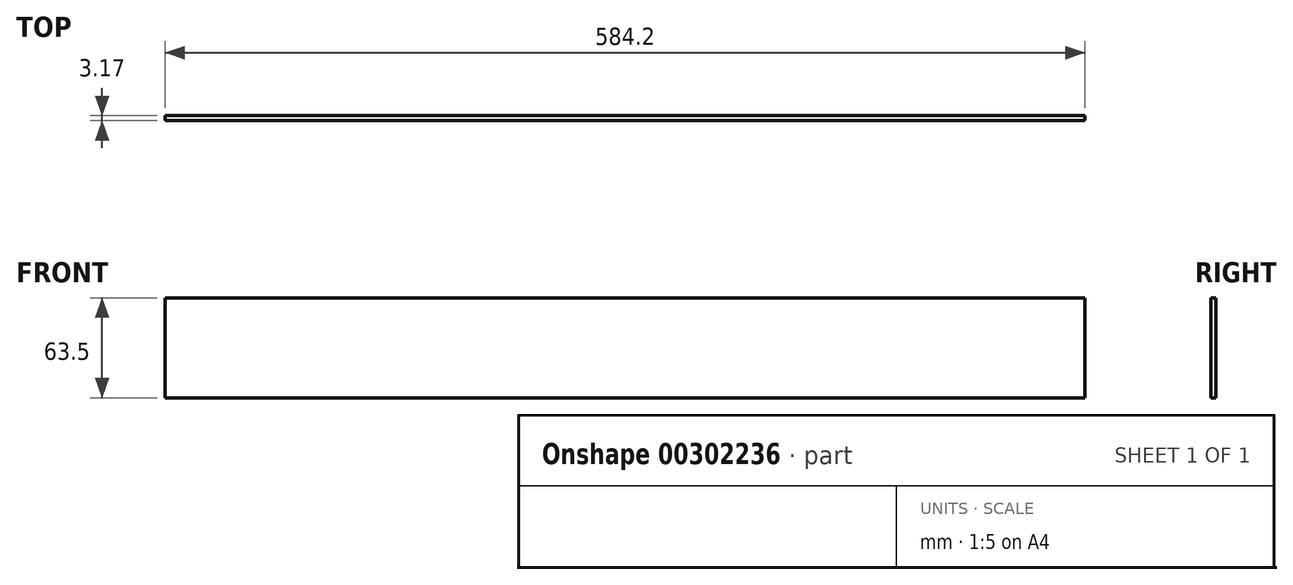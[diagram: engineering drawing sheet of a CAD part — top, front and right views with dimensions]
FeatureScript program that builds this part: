
annotation { "Feature Type Name" : "Feature", "Feature Type Description" : "" }
export const myFeature = defineFeature(function(context is Context, id is Id, definition is map)
    precondition{}
    {
        {
            var Q0;
            Q0=qCreatedBy(makeId("Front.planeOp"),FACE);
            var sketch = newSketch(context, id + "F0", { "sketchPlane" : qUnion([Q0])});
            skLineSegment(sketch, "E0.bottom", {"start": v(0, 0) * mm, "end": v(584.2, 0) * mm});
            skLineSegment(sketch, "E0.top", {"start": v(0, 63.5) * mm, "end": v(584.2, 63.5) * mm});
            skLineSegment(sketch, "E0.left", {"start": v(0, 0) * mm, "end": v(0, 63.5) * mm});
            skLineSegment(sketch, "E0.right", {"start": v(584.2, 0) * mm, "end": v(584.2, 63.5) * mm});
            skSolve(sketch);
        }
        {
            var Q0;
            Q0=makeQuery(id+"F0.imprint","IMPRINT",FACE,{"disambiguationData":[TD([[makeQuery(id+"F0.imprint","IMPRINT",EDGE,{"derivedFrom":sQuery(id+"F0.wireOp",EDGE,"E0.bottom")}),1.0]])]});
            extrude(context, id + "F1", {"entities" : qUnion([Q0]), "depth" : 3.17 * mm});
        }
    });
